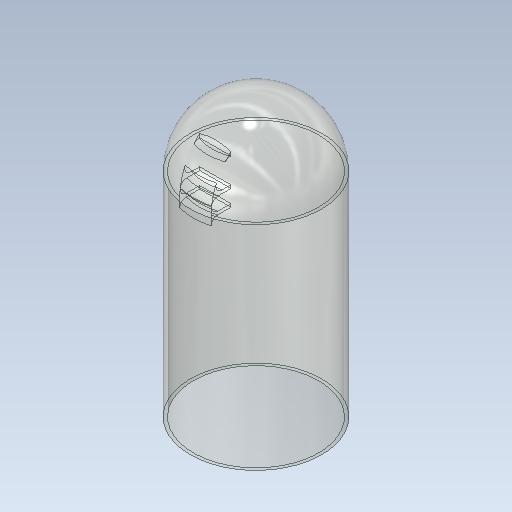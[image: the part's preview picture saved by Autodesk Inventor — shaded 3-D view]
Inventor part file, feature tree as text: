
AUTODESK INVENTOR PART (.ipt)
format: ipt  version: 2021 (Build 250183000, 183)  size: 302,592 bytes
history: native  units: mm
features: sketch x7, extrude x5, revolve x2, fillet x2, shell x1
ambient origin geometry x8: Origin, YZ Plane, XZ Plane, XY Plane, X Axis, Y Axis, Z Axis, Center Point
bodies: Solid2 (feature_tree)
feature tree (17):
  revolve  "Revolution3"  [1 undecoded]
  shell  "Vaciado5"  Thickness=21.0mm
  extrude  "Extrusión5"  Depth=1.0mm
  extrude  "Extrusión1"  Depth=12.0mm
  extrude  "Extrusión2"  Depth=2.0mm
  extrude  "Extrusión4"  Depth=20.0mm
  fillet  "Empalme2"  Radius=16.0mm
  extrude  "Extrusión6"  Depth=10.0mm
  revolve  "Revolución4"  [1 undecoded]
  fillet  "Empalme3"  Radius=20.0mm
  sketch  "Sketch3"  dims[d10=180.0deg d14=10.5mm d15=21.0mm]
  sketch  "Boceto5"  dims[d16=34.0mm d18=1.0mm]
  sketch  "Boceto6"  dims[d19=0.5mm d20=12.0mm]
  sketch  "Boceto8"  dims[d21=15.5mm d22=2.0mm]
  sketch  "Boceto9"  dims[d23=0.0mm d24=20.0mm d25=16.0mm]
  sketch  "Boceto10"  dims[d26=100.0mm d27=0.0mm d36=10.0mm]
  sketch  "Boceto11"  dims[d37=5.0mm d40=34.0mm d41=20.0mm d43=5.0mm d44=0.0mm d46=2.0mm d47=1.5mm d48=5.0mm d49=21.0mm d50=1.0mm d51=21.0mm d52=1.0mm d53=0.0mm d54=1.0mm d55=0.0mm d56=0.5mm d57=0.5mm d58=1.0mm d59=10.5mm d60=21.0mm d61=34.0mm d63=0.75mm d64=2.0mm d65=20.0mm d66=42.0mm d67=10.0mm d68=41.0mm d69=90.0deg d70=1.0mm]
note: 2 required parameter values undecoded (feature->parameter linkage not recoverable at this tier; creation-order binding heuristic only, values carry confidence <= 0.55)
